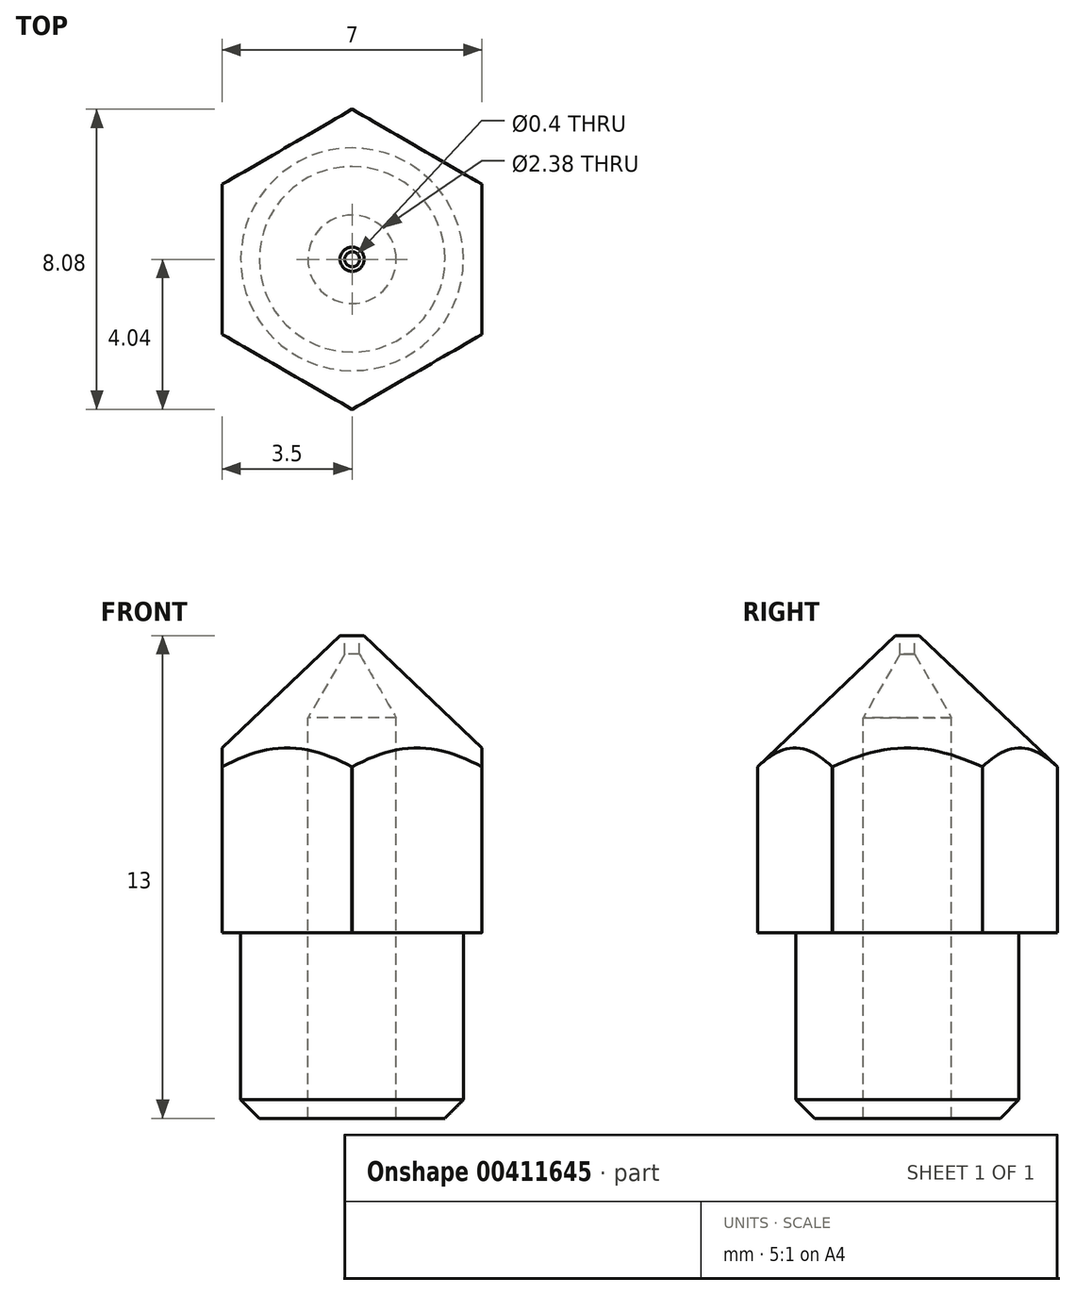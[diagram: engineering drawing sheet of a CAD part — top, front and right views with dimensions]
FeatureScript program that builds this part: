
annotation { "Feature Type Name" : "Feature", "Feature Type Description" : "" }
export const myFeature = defineFeature(function(context is Context, id is Id, definition is map)
    precondition{}
    {
        {
            var Q0;
            Q0=qCreatedBy(makeId("Front.planeOp"),FACE);
            var sketch = newSketch(context, id + "F0", { "sketchPlane" : qUnion([Q0])});
            skLineSegment(sketch, "E0", {"start": v(0, -5) * mm, "end": v(3, -5) * mm});
            skLineSegment(sketch, "E1", {"start": v(3, -5) * mm, "end": v(3, 0) * mm});
            skLineSegment(sketch, "E2", {"start": v(3, 0) * mm, "end": v(4.04, 0) * mm});
            skLineSegment(sketch, "E3", {"start": v(4.04, 0) * mm, "end": v(4.04, 4.46) * mm});
            skLineSegment(sketch, "E4", {"start": v(0, 6.21) * mm, "end": v(0, -4.68) * mm, "construction": true});
            skLineSegment(sketch, "E5.MirrorCS", {"start": v(-4.04, 0) * mm, "end": v(-4.04, 4.46) * mm});
            skLineSegment(sketch, "E6.MirrorCS", {"start": v(-3, 0) * mm, "end": v(-4.04, 0) * mm});
            skLineSegment(sketch, "E7.MirrorCS", {"start": v(-3, -5) * mm, "end": v(-3, 0) * mm});
            skLineSegment(sketch, "E8.MirrorCS", {"start": v(0, -5) * mm, "end": v(-3, -5) * mm});
            skLineSegment(sketch, "E9", {"start": v(4.04, 4.46) * mm, "end": v(0.33, 8) * mm});
            skLineSegment(sketch, "E10", {"start": v(0.33, 8) * mm, "end": v(0, 8) * mm});
            skLineSegment(sketch, "E11.MirrorCS", {"start": v(-4.04, 4.46) * mm, "end": v(-0.33, 8) * mm});
            skLineSegment(sketch, "E12.MirrorCS", {"start": v(-0.33, 8) * mm, "end": v(0, 8) * mm});
            skLineSegment(sketch, "E13", {"start": v(0.2, 8) * mm, "end": v(0.2, 7.5) * mm});
            skLineSegment(sketch, "E14.MirrorCS", {"start": v(-0.2, 8) * mm, "end": v(-0.2, 7.5) * mm});
            skLineSegment(sketch, "E15", {"start": v(-1, 7.5) * mm, "end": v(1.04, 7.5) * mm, "construction": true});
            skLineSegment(sketch, "E16", {"start": v(0.2, 7.5) * mm, "end": v(1.2, 5.79) * mm});
            skLineSegment(sketch, "E17", {"start": v(1.19, 5.79) * mm, "end": v(1.2, -5) * mm});
            skLineSegment(sketch, "E18.MirrorCS", {"start": v(-0.2, 7.5) * mm, "end": v(-1.19, 5.79) * mm});
            skLineSegment(sketch, "E19.MirrorCS", {"start": v(-1.2, 5.79) * mm, "end": v(-1.2, -5) * mm});
            skPoint(sketch, "E20.orphan", {"position": v(-0.2, -5) * mm});
            skPoint(sketch, "E21.orphan", {"position": v(0.2, -5) * mm});
            skLineSegment(sketch, "E22", {"start": v(-4.3, 5.79) * mm, "end": v(5.08, 5.79) * mm, "construction": true});
            skSolve(sketch);
        }
        {
            var Q0;
            {var subQ0=sQuery(id+"F0.wireOp",EDGE,"E1");Q0=makeQuery(id+"F0.imprint","IMPRINT",FACE,{"disambiguationData":[TD([[makeQuery(id+"F0.imprint","IMPRINT",EDGE,{"derivedFrom":subQ0}),1.0]])]});}
            var Q1;
            Q1=sQuery(id+"F0.wireOp",EDGE,"E4");
            revolve(context, id + "F1", {"entities" : qUnion([Q0]), "axis" : qUnion([Q1]), "revolveType" : RevolveType.FULL});
        }
        {
            var Q0;
            Q0=makeQuery(id+"F1.opRevolve","SWEPT_EDGE",EDGE,{"disambiguationData":[OSD([sQuery(id+"F0.wireOp",EDGE,"E0"),sQuery(id+"F0.wireOp",EDGE,"E1")])]});
            chamfer(context, id + "F2", {"entities" : qUnion([Q0]), "width" : 0.5 * mm, "tangentPropagation" : true});
        }
        {
            var Q0;
            Q0=makeQuery(id+"F1.opRevolve","SWEPT_FACE",FACE,{"disambiguationData":[OSD([sQuery(id+"F0.wireOp",EDGE,"E10")])]});
            var sketch = newSketch(context, id + "F3", { "sketchPlane" : qUnion([Q0])});
            skLineSegment(sketch, "E23.bottom", {"start": v(3.5, 4.65) * mm, "end": v(5.23, 4.65) * mm});
            skLineSegment(sketch, "E23.top", {"start": v(3.5, -4.77) * mm, "end": v(5.23, -4.77) * mm});
            skLineSegment(sketch, "E23.left", {"start": v(3.5, 4.65) * mm, "end": v(3.5, -4.77) * mm});
            skLineSegment(sketch, "E23.right", {"start": v(5.23, 4.65) * mm, "end": v(5.23, -4.77) * mm});
            skLineSegment(sketch, "E24.1.0", {"start": v(-2.28, 5.36) * mm, "end": v(5.88, 0.65) * mm});
            skLineSegment(sketch, "E24.1.1", {"start": v(-2.28, 5.36) * mm, "end": v(-1.41, 6.85) * mm});
            skLineSegment(sketch, "E24.1.2", {"start": v(-1.41, 6.85) * mm, "end": v(6.75, 2.14) * mm});
            skLineSegment(sketch, "E24.1.3", {"start": v(5.88, 0.65) * mm, "end": v(6.75, 2.14) * mm});
            skLineSegment(sketch, "E24.2.0", {"start": v(-5.78, 0.7) * mm, "end": v(2.38, 5.42) * mm});
            skLineSegment(sketch, "E24.2.1", {"start": v(-5.78, 0.7) * mm, "end": v(-6.64, 2.2) * mm});
            skLineSegment(sketch, "E24.2.2", {"start": v(-6.64, 2.2) * mm, "end": v(1.52, 6.91) * mm});
            skLineSegment(sketch, "E24.2.3", {"start": v(2.38, 5.42) * mm, "end": v(1.52, 6.91) * mm});
            skLineSegment(sketch, "E24.3.0", {"start": v(-3.5, -4.65) * mm, "end": v(-3.5, 4.77) * mm});
            skLineSegment(sketch, "E24.3.1", {"start": v(-3.5, -4.65) * mm, "end": v(-5.23, -4.65) * mm});
            skLineSegment(sketch, "E24.3.2", {"start": v(-5.23, -4.65) * mm, "end": v(-5.23, 4.77) * mm});
            skLineSegment(sketch, "E24.3.3", {"start": v(-3.5, 4.77) * mm, "end": v(-5.23, 4.77) * mm});
            skLineSegment(sketch, "E24.4.0", {"start": v(2.28, -5.36) * mm, "end": v(-5.88, -0.65) * mm});
            skLineSegment(sketch, "E24.4.1", {"start": v(2.28, -5.36) * mm, "end": v(1.41, -6.85) * mm});
            skLineSegment(sketch, "E24.4.2", {"start": v(1.41, -6.85) * mm, "end": v(-6.75, -2.14) * mm});
            skLineSegment(sketch, "E24.4.3", {"start": v(-5.88, -0.65) * mm, "end": v(-6.75, -2.14) * mm});
            skLineSegment(sketch, "E24.5.0", {"start": v(5.78, -0.7) * mm, "end": v(-2.38, -5.42) * mm});
            skLineSegment(sketch, "E24.5.1", {"start": v(5.78, -0.7) * mm, "end": v(6.64, -2.2) * mm});
            skLineSegment(sketch, "E24.5.2", {"start": v(6.64, -2.2) * mm, "end": v(-1.52, -6.91) * mm});
            skLineSegment(sketch, "E24.5.3", {"start": v(-2.38, -5.42) * mm, "end": v(-1.52, -6.91) * mm});
            skPoint(sketch, "E24.center", {"position": v(0, 0) * mm});
            skSolve(sketch);
        }
        {
            var Q0;
            Q0 = qSketchRegion(id + "F3", true);
            extrude(context, id + "F4", {"entities" : qUnion([Q0]), "operationType" : NewBodyOperationType.REMOVE, "endBound" : BoundingType.THROUGH_ALL, "oppositeDirection" : true, "depth" : 25 * mm});
        }
    });
